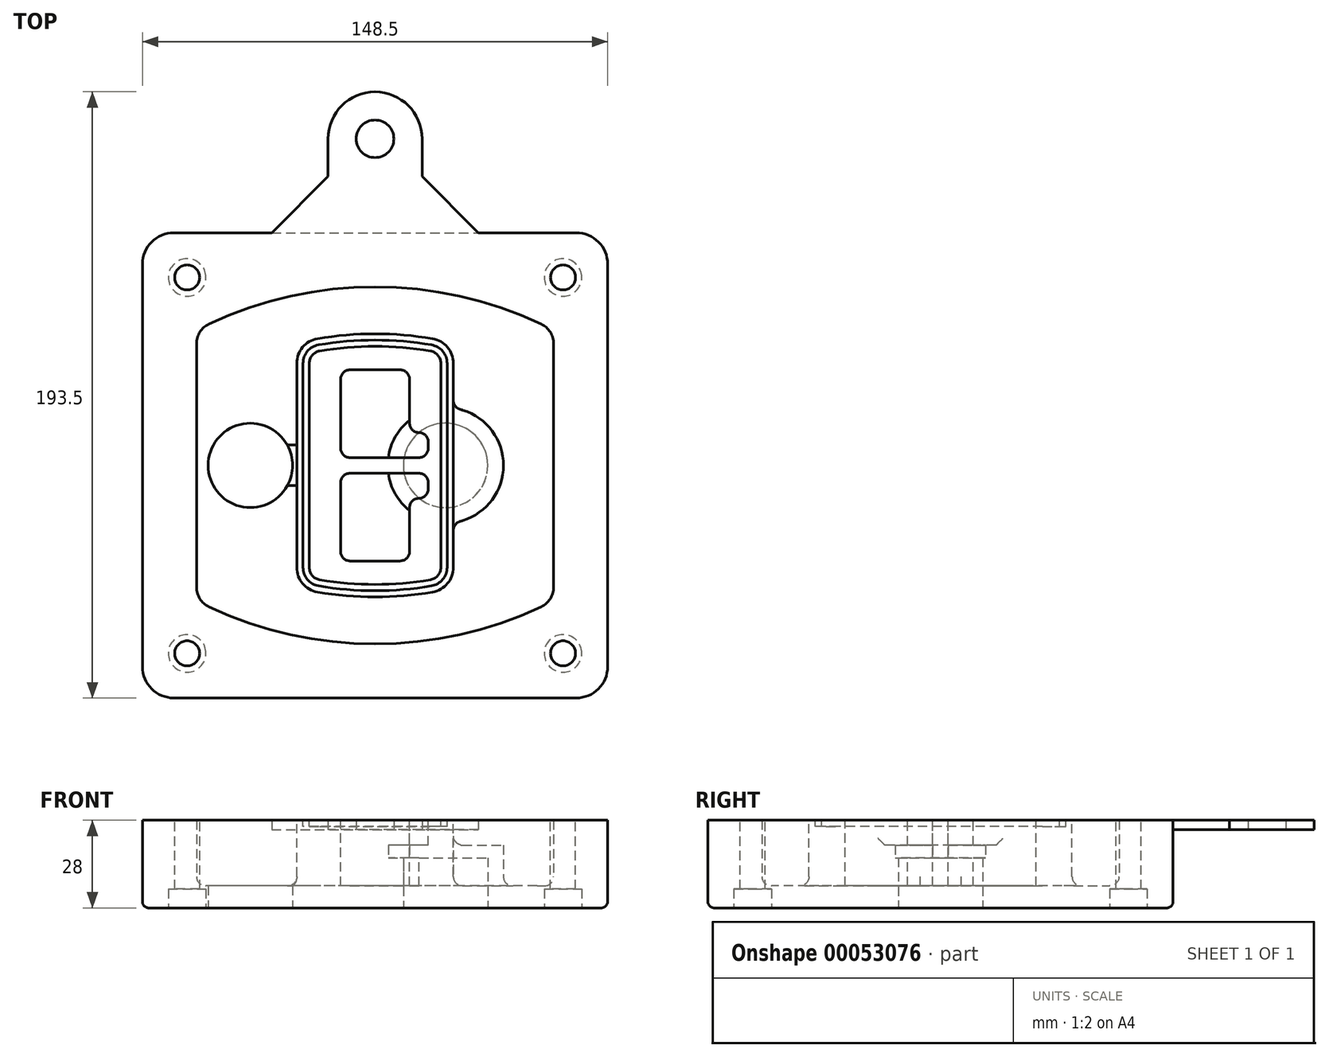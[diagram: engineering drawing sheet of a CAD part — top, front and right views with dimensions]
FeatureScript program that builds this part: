
annotation { "Feature Type Name" : "Feature", "Feature Type Description" : "" }
export const myFeature = defineFeature(function(context is Context, id is Id, definition is map)
    precondition{}
    {
        {
            var Q0;
            Q0=qCreatedBy(makeId("Top.planeOp"),FACE);
            var sketch = newSketch(context, id + "F0", { "sketchPlane" : qUnion([Q0])});
            skPoint(sketch, "E0.rect.middle", {"position": v(0, 0) * mm});
            skLineSegment(sketch, "E1.bottom", {"start": v(24.05, 28.38) * mm, "end": v(152.55, 28.38) * mm});
            skLineSegment(sketch, "E1.top", {"start": v(24.05, 176.88) * mm, "end": v(152.55, 176.88) * mm});
            skLineSegment(sketch, "E1.left", {"start": v(14.05, 38.38) * mm, "end": v(14.05, 166.88) * mm});
            skLineSegment(sketch, "E1.right", {"start": v(162.55, 38.38) * mm, "end": v(162.55, 166.88) * mm});
            skLineSegment(sketch, "E2", {"start": v(14.05, 176.88) * mm, "end": v(162.55, 28.38) * mm, "construction": true});
            skLineSegment(sketch, "E3", {"start": v(162.55, 176.88) * mm, "end": v(14.05, 28.38) * mm, "construction": true});
            skCircle(sketch, "E4", {"center": v(28.3, 162.63) * mm, "radius": 4 * mm});
            skCircle(sketch, "E5", {"center": v(148.3, 162.63) * mm, "radius": 4 * mm});
            skCircle(sketch, "E6", {"center": v(148.3, 42.63) * mm, "radius": 4 * mm});
            skCircle(sketch, "E7", {"center": v(28.3, 42.63) * mm, "radius": 4 * mm});
            skLineSegment(sketch, "E8", {"start": v(28.3, 162.63) * mm, "end": v(148.3, 162.63) * mm, "construction": true});
            skLineSegment(sketch, "E9", {"start": v(148.3, 162.63) * mm, "end": v(148.3, 42.63) * mm, "construction": true});
            skLineSegment(sketch, "E10", {"start": v(148.3, 42.63) * mm, "end": v(28.3, 42.63) * mm, "construction": true});
            skLineSegment(sketch, "E11", {"start": v(28.3, 42.63) * mm, "end": v(28.3, 162.63) * mm, "construction": true});
            skLineSegment(sketch, "E12", {"start": v(28.3, 141.46) * mm, "end": v(28.3, 63.8) * mm});
            skLineSegment(sketch, "E13", {"start": v(148.3, 141.46) * mm, "end": v(148.3, 63.8) * mm});
            skArc(sketch, "E14", {"start": v(142.56, 150.51) * mm, "mid": v(88.3, 162.63) * mm, "end": v(34.04, 150.51) * mm});
            skArc(sketch, "E15", {"start": v(34.04, 54.75) * mm, "mid": v(88.3, 42.63) * mm, "end": v(142.56, 54.75) * mm});
            skLineSegment(sketch, "E16", {"start": v(28.3, 102.63) * mm, "end": v(148.3, 102.63) * mm, "construction": true});
            skPoint(sketch, "E17.visualSharp", {"position": v(28.3, 57.63) * mm});
            skArc(sketch, "E17.filletArc", {"start": v(28.3, 63.8) * mm, "mid": v(29.86, 58.44) * mm, "end": v(34.04, 54.75) * mm});
            skPoint(sketch, "E18.visualSharp", {"position": v(28.3, 147.63) * mm});
            skArc(sketch, "E18.filletArc", {"start": v(34.04, 150.51) * mm, "mid": v(29.86, 146.82) * mm, "end": v(28.3, 141.46) * mm});
            skPoint(sketch, "E19.visualSharp", {"position": v(148.3, 147.63) * mm});
            skArc(sketch, "E19.filletArc", {"start": v(148.3, 141.46) * mm, "mid": v(146.74, 146.82) * mm, "end": v(142.56, 150.51) * mm});
            skPoint(sketch, "E20.visualSharp", {"position": v(148.3, 57.63) * mm});
            skArc(sketch, "E20.filletArc", {"start": v(142.56, 54.75) * mm, "mid": v(146.74, 58.44) * mm, "end": v(148.3, 63.8) * mm});
            skPoint(sketch, "E21.visualSharp", {"position": v(14.05, 176.88) * mm});
            skArc(sketch, "E21.filletArc", {"start": v(24.05, 176.88) * mm, "mid": v(16.98, 173.95) * mm, "end": v(14.05, 166.88) * mm});
            skPoint(sketch, "E22.visualSharp", {"position": v(162.55, 176.88) * mm});
            skArc(sketch, "E22.filletArc", {"start": v(162.55, 166.88) * mm, "mid": v(159.62, 173.95) * mm, "end": v(152.55, 176.88) * mm});
            skPoint(sketch, "E23.visualSharp", {"position": v(162.55, 28.38) * mm});
            skArc(sketch, "E23.filletArc", {"start": v(152.55, 28.38) * mm, "mid": v(159.62, 31.31) * mm, "end": v(162.55, 38.38) * mm});
            skPoint(sketch, "E24.visualSharp", {"position": v(14.05, 28.38) * mm});
            skArc(sketch, "E24.filletArc", {"start": v(14.05, 38.38) * mm, "mid": v(16.98, 31.31) * mm, "end": v(24.05, 28.38) * mm});
            skArc(sketch, "E25.0", {"start": v(145.3, 141.46) * mm, "mid": v(144.2, 145.22) * mm, "end": v(141.28, 147.8) * mm});
            skLineSegment(sketch, "E25.1", {"start": v(145.3, 141.46) * mm, "end": v(145.3, 63.8) * mm});
            skArc(sketch, "E25.2", {"start": v(141.28, 57.47) * mm, "mid": v(144.2, 60.05) * mm, "end": v(145.3, 63.8) * mm});
            skArc(sketch, "E25.3", {"start": v(35.32, 57.47) * mm, "mid": v(88.3, 45.63) * mm, "end": v(141.28, 57.47) * mm});
            skArc(sketch, "E25.4", {"start": v(31.3, 63.8) * mm, "mid": v(32.4, 60.05) * mm, "end": v(35.32, 57.47) * mm});
            skArc(sketch, "E25.5", {"start": v(141.28, 147.8) * mm, "mid": v(88.3, 159.63) * mm, "end": v(35.32, 147.8) * mm});
            skLineSegment(sketch, "E25.6", {"start": v(31.3, 141.46) * mm, "end": v(31.3, 63.8) * mm});
            skArc(sketch, "E25.7", {"start": v(35.32, 147.8) * mm, "mid": v(32.4, 145.22) * mm, "end": v(31.3, 141.46) * mm});
            skArc(sketch, "E26.0", {"start": v(32.34, 154.13) * mm, "mid": v(26.48, 148.97) * mm, "end": v(24.3, 141.46) * mm});
            skArc(sketch, "E26.1", {"start": v(144.26, 154.13) * mm, "mid": v(88.3, 166.63) * mm, "end": v(32.34, 154.13) * mm});
            skArc(sketch, "E26.2", {"start": v(152.3, 141.46) * mm, "mid": v(150.12, 148.97) * mm, "end": v(144.26, 154.13) * mm});
            skLineSegment(sketch, "E26.3", {"start": v(152.3, 141.46) * mm, "end": v(152.3, 63.8) * mm});
            skArc(sketch, "E26.4", {"start": v(144.26, 51.13) * mm, "mid": v(150.12, 56.3) * mm, "end": v(152.3, 63.8) * mm});
            skLineSegment(sketch, "E26.5", {"start": v(24.3, 141.46) * mm, "end": v(24.3, 63.8) * mm});
            skArc(sketch, "E26.6", {"start": v(32.34, 51.13) * mm, "mid": v(88.3, 38.63) * mm, "end": v(144.26, 51.13) * mm});
            skArc(sketch, "E26.7", {"start": v(24.3, 63.8) * mm, "mid": v(26.48, 56.3) * mm, "end": v(32.34, 51.13) * mm});
            skSolve(sketch);
        }
        {
            var Q0;
            Q0=makeQuery(id+"F0.imprint","IMPRINT",FACE,{"disambiguationData":[TD([[makeQuery(id+"F0.imprint","IMPRINT",EDGE,{"derivedFrom":sQuery(id+"F0.wireOp",EDGE,"E1.bottom")}),1.0]])]});
            var Q1;
            Q1=makeQuery(id+"F0.imprint","IMPRINT",FACE,{"disambiguationData":[TD([[makeQuery(id+"F0.imprint","IMPRINT",EDGE,{"derivedFrom":sQuery(id+"F0.wireOp",EDGE,"E12")}),1.0]])]});
            var Q2;
            Q2=makeQuery(id+"F0.imprint","IMPRINT",FACE,{"disambiguationData":[TD([[makeQuery(id+"F0.imprint","IMPRINT",EDGE,{"derivedFrom":sQuery(id+"F0.wireOp",EDGE,"E25.0")}),1.0]])]});
            var Q3;
            Q3=makeQuery(id+"F0.imprint","IMPRINT",FACE,{"disambiguationData":[TD([[makeQuery(id+"F0.imprint","IMPRINT",EDGE,{"derivedFrom":sQuery(id+"F0.wireOp",EDGE,"E12")}),-1.0]])]});
            extrude(context, id + "F1", {"entities" : qUnion([Q0, Q1, Q2, Q3]), "oppositeDirection" : true, "depth" : 25 * mm});
        }
        {
            var Q0;
            Q0=makeQuery(id+"F0.imprint","IMPRINT",FACE,{"disambiguationData":[TD([[makeQuery(id+"F0.imprint","IMPRINT",EDGE,{"derivedFrom":sQuery(id+"F0.wireOp",EDGE,"E12")}),1.0]])]});
            extrude(context, id + "F2", {"entities" : qUnion([Q0]), "operationType" : NewBodyOperationType.ADD, "depth" : 3 * mm});
        }
        {
            var Q0;
            Q0=makeQuery(id+"F0.imprint","IMPRINT",FACE,{"disambiguationData":[TD([[makeQuery(id+"F0.imprint","IMPRINT",EDGE,{"derivedFrom":sQuery(id+"F0.wireOp",EDGE,"E25.0")}),1.0]])]});
            extrude(context, id + "F3", {"entities" : qUnion([Q0]), "operationType" : NewBodyOperationType.REMOVE, "oppositeDirection" : true, "depth" : 18 * mm});
        }
        {
            var Q0;
            Q0=makeQuery(id+"F2.opExtrude","CAP_FACE",FACE,{"disambiguationData":[OSD([sQuery(id+"F0.wireOp",EDGE,"E12"),sQuery(id+"F0.wireOp",EDGE,"E13"),sQuery(id+"F0.wireOp",EDGE,"E14"),sQuery(id+"F0.wireOp",EDGE,"E15"),sQuery(id+"F0.wireOp",EDGE,"E17.filletArc"),sQuery(id+"F0.wireOp",EDGE,"E18.filletArc"),sQuery(id+"F0.wireOp",EDGE,"E19.filletArc"),sQuery(id+"F0.wireOp",EDGE,"E20.filletArc"),sQuery(id+"F0.wireOp",EDGE,"E25.0"),sQuery(id+"F0.wireOp",EDGE,"E25.1"),sQuery(id+"F0.wireOp",EDGE,"E25.2"),sQuery(id+"F0.wireOp",EDGE,"E25.3"),sQuery(id+"F0.wireOp",EDGE,"E25.4"),sQuery(id+"F0.wireOp",EDGE,"E25.5"),sQuery(id+"F0.wireOp",EDGE,"E25.6"),sQuery(id+"F0.wireOp",EDGE,"E25.7")])],"isStart":false});
            var sketch = newSketch(context, id + "F4", { "sketchPlane" : qUnion([Q0])});
            skArc(sketch, "E27.0", {"start": v(69.96, 62.18) * mm, "mid": v(88.3, 60.63) * mm, "end": v(106.64, 62.18) * mm});
            skArc(sketch, "E28.0", {"start": v(106.64, 143.09) * mm, "mid": v(88.3, 144.63) * mm, "end": v(69.96, 143.09) * mm});
            skLineSegment(sketch, "E29", {"start": v(63.3, 135.2) * mm, "end": v(63.3, 70.07) * mm});
            skLineSegment(sketch, "E30", {"start": v(113.3, 135.2) * mm, "end": v(113.3, 70.07) * mm});
            skLineSegment(sketch, "E31", {"start": v(63.3, 141.74) * mm, "end": v(113.3, 141.74) * mm, "construction": true});
            skLineSegment(sketch, "E32", {"start": v(63.3, 63.52) * mm, "end": v(113.3, 63.52) * mm, "construction": true});
            skPoint(sketch, "E33.visualSharp", {"position": v(63.3, 141.74) * mm});
            skArc(sketch, "E33.filletArc", {"start": v(69.96, 143.09) * mm, "mid": v(65.19, 140.36) * mm, "end": v(63.3, 135.2) * mm});
            skPoint(sketch, "E34.visualSharp", {"position": v(113.3, 141.74) * mm});
            skArc(sketch, "E34.filletArc", {"start": v(113.3, 135.2) * mm, "mid": v(111.41, 140.36) * mm, "end": v(106.64, 143.09) * mm});
            skPoint(sketch, "E35.visualSharp", {"position": v(113.3, 63.52) * mm});
            skArc(sketch, "E35.filletArc", {"start": v(106.64, 62.18) * mm, "mid": v(111.41, 64.9) * mm, "end": v(113.3, 70.07) * mm});
            skPoint(sketch, "E36.visualSharp", {"position": v(63.3, 63.52) * mm});
            skArc(sketch, "E36.filletArc", {"start": v(63.3, 70.07) * mm, "mid": v(65.19, 64.9) * mm, "end": v(69.96, 62.18) * mm});
            skArc(sketch, "E37.0", {"start": v(141.28, 147.8) * mm, "mid": v(88.3, 159.63) * mm, "end": v(35.32, 147.8) * mm});
            skArc(sketch, "E37.1", {"start": v(35.32, 147.8) * mm, "mid": v(32.4, 145.22) * mm, "end": v(31.3, 141.46) * mm});
            skLineSegment(sketch, "E37.2", {"start": v(31.3, 141.46) * mm, "end": v(31.3, 63.8) * mm});
            skArc(sketch, "E37.3", {"start": v(31.3, 63.8) * mm, "mid": v(32.4, 60.05) * mm, "end": v(35.32, 57.47) * mm});
            skArc(sketch, "E37.4", {"start": v(35.32, 57.47) * mm, "mid": v(88.3, 45.63) * mm, "end": v(141.28, 57.47) * mm});
            skArc(sketch, "E37.5", {"start": v(141.28, 57.47) * mm, "mid": v(144.2, 60.05) * mm, "end": v(145.3, 63.8) * mm});
            skLineSegment(sketch, "E37.6", {"start": v(145.3, 141.46) * mm, "end": v(145.3, 63.8) * mm});
            skArc(sketch, "E37.7", {"start": v(145.3, 141.46) * mm, "mid": v(144.2, 145.22) * mm, "end": v(141.28, 147.8) * mm});
            skLineSegment(sketch, "E38.0", {"start": v(111.3, 135.2) * mm, "end": v(111.3, 70.07) * mm});
            skArc(sketch, "E38.1", {"start": v(106.3, 64.15) * mm, "mid": v(109.88, 66.2) * mm, "end": v(111.3, 70.07) * mm});
            skArc(sketch, "E38.2", {"start": v(70.3, 64.15) * mm, "mid": v(88.3, 62.63) * mm, "end": v(106.3, 64.15) * mm});
            skArc(sketch, "E38.3", {"start": v(65.3, 70.07) * mm, "mid": v(66.72, 66.2) * mm, "end": v(70.3, 64.15) * mm});
            skLineSegment(sketch, "E38.4", {"start": v(65.3, 135.2) * mm, "end": v(65.3, 70.07) * mm});
            skArc(sketch, "E38.5", {"start": v(111.3, 135.2) * mm, "mid": v(109.88, 139.07) * mm, "end": v(106.3, 141.11) * mm});
            skArc(sketch, "E38.6", {"start": v(70.3, 141.11) * mm, "mid": v(66.72, 139.07) * mm, "end": v(65.3, 135.2) * mm});
            skArc(sketch, "E38.7", {"start": v(106.3, 141.11) * mm, "mid": v(88.3, 142.63) * mm, "end": v(70.3, 141.11) * mm});
            skArc(sketch, "E39.0", {"start": v(109.3, 135.2) * mm, "mid": v(108.36, 137.78) * mm, "end": v(105.97, 139.14) * mm});
            skLineSegment(sketch, "E39.1", {"start": v(109.3, 135.2) * mm, "end": v(109.3, 70.07) * mm});
            skArc(sketch, "E39.2", {"start": v(105.97, 66.12) * mm, "mid": v(108.36, 67.49) * mm, "end": v(109.3, 70.07) * mm});
            skArc(sketch, "E39.3", {"start": v(70.63, 66.12) * mm, "mid": v(88.3, 64.63) * mm, "end": v(105.97, 66.12) * mm});
            skArc(sketch, "E39.4", {"start": v(67.3, 70.07) * mm, "mid": v(68.24, 67.49) * mm, "end": v(70.63, 66.12) * mm});
            skArc(sketch, "E39.5", {"start": v(105.97, 139.14) * mm, "mid": v(88.3, 140.63) * mm, "end": v(70.63, 139.14) * mm});
            skLineSegment(sketch, "E39.6", {"start": v(67.3, 135.2) * mm, "end": v(67.3, 70.07) * mm});
            skArc(sketch, "E39.7", {"start": v(70.63, 139.14) * mm, "mid": v(68.24, 137.78) * mm, "end": v(67.3, 135.2) * mm});
            skLineSegment(sketch, "E40", {"start": v(63.3, 102.63) * mm, "end": v(113.3, 102.63) * mm, "construction": true});
            skLineSegment(sketch, "E41", {"start": v(77.3, 108.13) * mm, "end": v(77.3, 130.13) * mm});
            skLineSegment(sketch, "E42", {"start": v(80.3, 133.13) * mm, "end": v(96.3, 133.13) * mm});
            skLineSegment(sketch, "E43", {"start": v(99.3, 130.13) * mm, "end": v(99.3, 116.13) * mm});
            skLineSegment(sketch, "E44", {"start": v(102.3, 113.13) * mm, "end": v(102.3, 113.13) * mm});
            skLineSegment(sketch, "E45", {"start": v(105.3, 110.13) * mm, "end": v(105.3, 108.13) * mm});
            skLineSegment(sketch, "E46", {"start": v(102.3, 105.13) * mm, "end": v(80.3, 105.13) * mm});
            skPoint(sketch, "E47.visualSharp", {"position": v(77.3, 133.13) * mm});
            skArc(sketch, "E47.filletArc", {"start": v(80.3, 133.13) * mm, "mid": v(78.18, 132.25) * mm, "end": v(77.3, 130.13) * mm});
            skPoint(sketch, "E48.visualSharp", {"position": v(99.3, 133.13) * mm});
            skArc(sketch, "E48.filletArc", {"start": v(99.3, 130.13) * mm, "mid": v(98.42, 132.25) * mm, "end": v(96.3, 133.13) * mm});
            skPoint(sketch, "E49.visualSharp", {"position": v(99.3, 113.13) * mm});
            skArc(sketch, "E49.filletArc", {"start": v(99.3, 116.13) * mm, "mid": v(100.18, 114.01) * mm, "end": v(102.3, 113.13) * mm});
            skPoint(sketch, "E50.visualSharp", {"position": v(105.3, 113.13) * mm});
            skArc(sketch, "E50.filletArc", {"start": v(105.3, 110.13) * mm, "mid": v(104.42, 112.25) * mm, "end": v(102.3, 113.13) * mm});
            skPoint(sketch, "E51.visualSharp", {"position": v(105.3, 105.13) * mm});
            skArc(sketch, "E51.filletArc", {"start": v(102.3, 105.13) * mm, "mid": v(104.42, 106.01) * mm, "end": v(105.3, 108.13) * mm});
            skPoint(sketch, "E52.visualSharp", {"position": v(77.3, 105.13) * mm});
            skArc(sketch, "E52.filletArc", {"start": v(77.3, 108.13) * mm, "mid": v(78.18, 106.01) * mm, "end": v(80.3, 105.13) * mm});
            skLineSegment(sketch, "E53.0.MirrorCS", {"start": v(102.3, 100.13) * mm, "end": v(80.3, 100.13) * mm});
            skArc(sketch, "E54.0.MirrorCS", {"start": v(77.3, 97.13) * mm, "mid": v(78.18, 99.25) * mm, "end": v(80.3, 100.13) * mm});
            skLineSegment(sketch, "E55.0.MirrorCS", {"start": v(77.3, 97.13) * mm, "end": v(77.3, 75.13) * mm});
            skArc(sketch, "E56.0.MirrorCS", {"start": v(80.3, 72.13) * mm, "mid": v(78.18, 73.01) * mm, "end": v(77.3, 75.13) * mm});
            skLineSegment(sketch, "E57.0.MirrorCS", {"start": v(80.3, 72.13) * mm, "end": v(96.3, 72.13) * mm});
            skArc(sketch, "E58.0.MirrorCS", {"start": v(99.3, 75.13) * mm, "mid": v(98.42, 73.01) * mm, "end": v(96.3, 72.13) * mm});
            skLineSegment(sketch, "E59.0.MirrorCS", {"start": v(99.3, 75.13) * mm, "end": v(99.3, 89.13) * mm});
            skArc(sketch, "E60.0.MirrorCS", {"start": v(99.3, 89.13) * mm, "mid": v(100.18, 91.25) * mm, "end": v(102.3, 92.13) * mm});
            skArc(sketch, "E61.0.MirrorCS", {"start": v(105.3, 95.13) * mm, "mid": v(104.42, 93.01) * mm, "end": v(102.3, 92.13) * mm});
            skLineSegment(sketch, "E62.0.MirrorCS", {"start": v(105.3, 95.13) * mm, "end": v(105.3, 97.13) * mm});
            skArc(sketch, "E63.0.MirrorCS", {"start": v(102.3, 100.13) * mm, "mid": v(104.42, 99.25) * mm, "end": v(105.3, 97.13) * mm});
            skSolve(sketch);
        }
        {
            var Q0;
            Q0=makeQuery(id+"F4.imprint","IMPRINT",FACE,{"disambiguationData":[TD([[makeQuery(id+"F4.imprint","IMPRINT",EDGE,{"derivedFrom":sQuery(id+"F4.wireOp",EDGE,"E27.0")}),1.0]])]});
            var Q1;
            Q1=makeQuery(id+"F4.imprint","IMPRINT",FACE,{"disambiguationData":[TD([[makeQuery(id+"F4.imprint","IMPRINT",EDGE,{"derivedFrom":sQuery(id+"F4.wireOp",EDGE,"E38.0")}),-1.0]])]});
            var Q2;
            Q2=makeQuery(id+"F4.imprint","IMPRINT",FACE,{"disambiguationData":[TD([[makeQuery(id+"F4.imprint","IMPRINT",EDGE,{"derivedFrom":sQuery(id+"F4.wireOp",EDGE,"E39.0")}),1.0]])]});
            extrude(context, id + "F5", {"entities" : qUnion([Q0, Q1, Q2]), "operationType" : NewBodyOperationType.ADD, "endBound" : BoundingType.UP_TO_NEXT, "oppositeDirection" : true, "depth" : 25 * mm});
        }
        {
            var Q0;
            Q0=makeQuery(id+"F4.imprint","IMPRINT",FACE,{"disambiguationData":[TD([[makeQuery(id+"F4.imprint","IMPRINT",EDGE,{"derivedFrom":sQuery(id+"F4.wireOp",EDGE,"E38.0")}),-1.0]])]});
            extrude(context, id + "F6", {"entities" : qUnion([Q0]), "operationType" : NewBodyOperationType.REMOVE, "oppositeDirection" : true, "depth" : 2 * mm});
        }
        {
            var Q0;
            Q0=makeQuery(id+"F1.opExtrude","CAP_FACE",FACE,{"disambiguationData":[OSD([sQuery(id+"F0.wireOp",EDGE,"E1.bottom"),sQuery(id+"F0.wireOp",EDGE,"E1.top"),sQuery(id+"F0.wireOp",EDGE,"E1.left"),sQuery(id+"F0.wireOp",EDGE,"E1.right"),sQuery(id+"F0.wireOp",EDGE,"E4"),sQuery(id+"F0.wireOp",EDGE,"E5"),sQuery(id+"F0.wireOp",EDGE,"E6"),sQuery(id+"F0.wireOp",EDGE,"E7"),sQuery(id+"F0.wireOp",EDGE,"E21.filletArc"),sQuery(id+"F0.wireOp",EDGE,"E22.filletArc"),sQuery(id+"F0.wireOp",EDGE,"E23.filletArc"),sQuery(id+"F0.wireOp",EDGE,"E24.filletArc")])],"isStart":false});
            var sketch = newSketch(context, id + "F7", { "sketchPlane" : qUnion([Q0])});
            skCircle(sketch, "E64", {"center": v(110.8, -102.63) * mm, "radius": 13.47 * mm});
            skCircle(sketch, "E65", {"center": v(48.49, -102.63) * mm, "radius": 13.47 * mm});
            skLineSegment(sketch, "E66", {"start": v(162.55, -102.63) * mm, "end": v(14.05, -102.63) * mm});
            skCircle(sketch, "E67", {"center": v(110.8, -102.63) * mm, "radius": 18.47 * mm});
            skCircle(sketch, "E68", {"center": v(148.3, -162.63) * mm, "radius": 6 * mm});
            skCircle(sketch, "E69", {"center": v(28.3, -162.63) * mm, "radius": 6 * mm});
            skCircle(sketch, "E70", {"center": v(28.3, -42.63) * mm, "radius": 6 * mm});
            skCircle(sketch, "E71", {"center": v(148.3, -42.63) * mm, "radius": 6 * mm});
            skSolve(sketch);
        }
        {
            var Q0;
            {var subQ1=sQuery(id+"F7.wireOp",EDGE,"E66");var subQ4=sQuery(id+"F7.wireOp",EDGE,"E64");var subQ6=makeQuery(id+"F7.imprint","INTERSECT",VERTEX,{"disambiguationData":[OD(0.0)],"derivedFrom":[subQ4,subQ1]});Q0=makeQuery(id+"F7.imprint","IMPRINT",FACE,{"disambiguationData":[TD([[makeQuery(id+"F7.imprint","IMPRINT",EDGE,{"disambiguationData":[TD([[subQ6,-1.0]])],"derivedFrom":subQ4}),-1.0]])]});}
            var Q1;
            {var subQ0=sQuery(id+"F7.wireOp",EDGE,"E66");var subQ1=sQuery(id+"F7.wireOp",EDGE,"E64");var subQ3=makeQuery(id+"F7.imprint","INTERSECT",VERTEX,{"disambiguationData":[OD(0.0)],"derivedFrom":[subQ1,subQ0]});Q1=makeQuery(id+"F7.imprint","IMPRINT",FACE,{"disambiguationData":[TD([[makeQuery(id+"F7.imprint","IMPRINT",EDGE,{"disambiguationData":[TD([[subQ3,-1.0]])],"derivedFrom":subQ1}),1.0]])]});}
            var Q2;
            {var subQ0=sQuery(id+"F7.wireOp",EDGE,"E66");var subQ1=sQuery(id+"F7.wireOp",EDGE,"E64");var subQ3=makeQuery(id+"F7.imprint","INTERSECT",VERTEX,{"disambiguationData":[OD(0.0)],"derivedFrom":[subQ1,subQ0]});Q2=makeQuery(id+"F7.imprint","IMPRINT",FACE,{"disambiguationData":[TD([[makeQuery(id+"F7.imprint","IMPRINT",EDGE,{"disambiguationData":[TD([[subQ3,1.0]])],"derivedFrom":subQ1}),1.0]])]});}
            var Q3;
            {var subQ1=sQuery(id+"F7.wireOp",EDGE,"E66");var subQ4=sQuery(id+"F7.wireOp",EDGE,"E64");var subQ6=makeQuery(id+"F7.imprint","INTERSECT",VERTEX,{"disambiguationData":[OD(0.0)],"derivedFrom":[subQ4,subQ1]});Q3=makeQuery(id+"F7.imprint","IMPRINT",FACE,{"disambiguationData":[TD([[makeQuery(id+"F7.imprint","IMPRINT",EDGE,{"disambiguationData":[TD([[subQ6,1.0]])],"derivedFrom":subQ4}),-1.0]])]});}
            extrude(context, id + "F8", {"entities" : qUnion([Q0, Q1, Q2, Q3]), "operationType" : NewBodyOperationType.ADD, "oppositeDirection" : true, "depth" : 20 * mm});
        }
        {
            var Q0;
            {var subQ0=sQuery(id+"F7.wireOp",EDGE,"E66");var subQ1=sQuery(id+"F7.wireOp",EDGE,"E64");var subQ3=makeQuery(id+"F7.imprint","INTERSECT",VERTEX,{"disambiguationData":[OD(0.0)],"derivedFrom":[subQ1,subQ0]});Q0=makeQuery(id+"F7.imprint","IMPRINT",FACE,{"disambiguationData":[TD([[makeQuery(id+"F7.imprint","IMPRINT",EDGE,{"disambiguationData":[TD([[subQ3,-1.0]])],"derivedFrom":subQ1}),1.0]])]});}
            var Q1;
            {var subQ0=sQuery(id+"F7.wireOp",EDGE,"E66");var subQ1=sQuery(id+"F7.wireOp",EDGE,"E64");var subQ3=makeQuery(id+"F7.imprint","INTERSECT",VERTEX,{"disambiguationData":[OD(0.0)],"derivedFrom":[subQ1,subQ0]});Q1=makeQuery(id+"F7.imprint","IMPRINT",FACE,{"disambiguationData":[TD([[makeQuery(id+"F7.imprint","IMPRINT",EDGE,{"disambiguationData":[TD([[subQ3,1.0]])],"derivedFrom":subQ1}),1.0]])]});}
            extrude(context, id + "F9", {"entities" : qUnion([Q0, Q1]), "operationType" : NewBodyOperationType.REMOVE, "oppositeDirection" : true, "depth" : 16 * mm});
        }
        {
            var Q0;
            {var subQ0=sQuery(id+"F7.wireOp",EDGE,"E66");var subQ1=sQuery(id+"F7.wireOp",EDGE,"E65");var subQ3=makeQuery(id+"F7.imprint","INTERSECT",VERTEX,{"disambiguationData":[OD(0.0)],"derivedFrom":[subQ1,subQ0]});Q0=makeQuery(id+"F7.imprint","IMPRINT",FACE,{"disambiguationData":[TD([[makeQuery(id+"F7.imprint","IMPRINT",EDGE,{"disambiguationData":[TD([[subQ3,-1.0]])],"derivedFrom":subQ1}),1.0]])]});}
            var Q1;
            {var subQ0=sQuery(id+"F7.wireOp",EDGE,"E66");var subQ1=sQuery(id+"F7.wireOp",EDGE,"E65");var subQ3=makeQuery(id+"F7.imprint","INTERSECT",VERTEX,{"disambiguationData":[OD(0.0)],"derivedFrom":[subQ1,subQ0]});Q1=makeQuery(id+"F7.imprint","IMPRINT",FACE,{"disambiguationData":[TD([[makeQuery(id+"F7.imprint","IMPRINT",EDGE,{"disambiguationData":[TD([[subQ3,1.0]])],"derivedFrom":subQ1}),1.0]])]});}
            extrude(context, id + "F10", {"entities" : qUnion([Q0, Q1]), "operationType" : NewBodyOperationType.REMOVE, "oppositeDirection" : true, "depth" : 25 * mm});
        }
        {
            var Q0;
            Q0=makeQuery(id+"F7.imprint","IMPRINT",FACE,{"disambiguationData":[TD([[makeQuery(id+"F7.imprint","IMPRINT",EDGE,{"derivedFrom":sQuery(id+"F7.wireOp",EDGE,"E68")}),1.0]])]});
            var Q1;
            Q1=makeQuery(id+"F7.imprint","IMPRINT",FACE,{"disambiguationData":[TD([[makeQuery(id+"F7.imprint","IMPRINT",EDGE,{"derivedFrom":makeQuery(id+"F1.opExtrude","CAP_EDGE",EDGE,{"disambiguationData":[OSD([sQuery(id+"F0.wireOp",EDGE,"E5")])],"isStart":false})}),-1.0]])]});
            var Q2;
            Q2=makeQuery(id+"F7.imprint","IMPRINT",FACE,{"disambiguationData":[TD([[makeQuery(id+"F7.imprint","IMPRINT",EDGE,{"derivedFrom":sQuery(id+"F7.wireOp",EDGE,"E69")}),1.0]])]});
            var Q3;
            Q3=makeQuery(id+"F7.imprint","IMPRINT",FACE,{"disambiguationData":[TD([[makeQuery(id+"F7.imprint","IMPRINT",EDGE,{"derivedFrom":makeQuery(id+"F1.opExtrude","CAP_EDGE",EDGE,{"disambiguationData":[OSD([sQuery(id+"F0.wireOp",EDGE,"E4")])],"isStart":false})}),-1.0]])]});
            var Q4;
            Q4=makeQuery(id+"F7.imprint","IMPRINT",FACE,{"disambiguationData":[TD([[makeQuery(id+"F7.imprint","IMPRINT",EDGE,{"derivedFrom":sQuery(id+"F7.wireOp",EDGE,"E70")}),1.0]])]});
            var Q5;
            Q5=makeQuery(id+"F7.imprint","IMPRINT",FACE,{"disambiguationData":[TD([[makeQuery(id+"F7.imprint","IMPRINT",EDGE,{"derivedFrom":makeQuery(id+"F1.opExtrude","CAP_EDGE",EDGE,{"disambiguationData":[OSD([sQuery(id+"F0.wireOp",EDGE,"E7")])],"isStart":false})}),-1.0]])]});
            var Q6;
            Q6=makeQuery(id+"F7.imprint","IMPRINT",FACE,{"disambiguationData":[TD([[makeQuery(id+"F7.imprint","IMPRINT",EDGE,{"derivedFrom":sQuery(id+"F7.wireOp",EDGE,"E71")}),1.0]])]});
            var Q7;
            Q7=makeQuery(id+"F7.imprint","IMPRINT",FACE,{"disambiguationData":[TD([[makeQuery(id+"F7.imprint","IMPRINT",EDGE,{"derivedFrom":makeQuery(id+"F1.opExtrude","CAP_EDGE",EDGE,{"disambiguationData":[OSD([sQuery(id+"F0.wireOp",EDGE,"E6")])],"isStart":false})}),-1.0]])]});
            extrude(context, id + "F11", {"entities" : qUnion([Q0, Q1, Q2, Q3, Q4, Q5, Q6, Q7]), "operationType" : NewBodyOperationType.REMOVE, "oppositeDirection" : true, "depth" : 6 * mm});
        }
        {
            var Q0;
            Q0=makeQuery(id+"F9.boolean.opBoolean","COPY",FACE,{"derivedFrom":makeQuery(id+"F9.opExtrude","CAP_FACE",FACE,{"disambiguationData":[OSD([sQuery(id+"F7.wireOp",EDGE,"E64")])],"isStart":false})});
            var sketch = newSketch(context, id + "F12", { "sketchPlane" : qUnion([Q0])});
            skArc(sketch, "E72.0", {"start": v(99.3, -88.19) * mm, "mid": v(94.75, -93.5) * mm, "end": v(92.5, -100.13) * mm});
            skArc(sketch, "E72.1", {"start": v(92.5, -105.13) * mm, "mid": v(94.75, -111.76) * mm, "end": v(99.3, -117.08) * mm});
            skLineSegment(sketch, "E73", {"start": v(92.5, -105.13) * mm, "end": v(102.3, -105.13) * mm});
            skLineSegment(sketch, "E74.0", {"start": v(102.3, -100.13) * mm, "end": v(92.5, -100.13) * mm});
            skArc(sketch, "E74.1", {"start": v(102.3, -100.13) * mm, "mid": v(104.42, -99.25) * mm, "end": v(105.3, -97.13) * mm});
            skLineSegment(sketch, "E74.2", {"start": v(105.3, -95.13) * mm, "end": v(105.3, -97.13) * mm});
            skArc(sketch, "E74.3", {"start": v(105.3, -95.13) * mm, "mid": v(104.42, -93.01) * mm, "end": v(102.3, -92.13) * mm});
            skArc(sketch, "E74.4", {"start": v(99.3, -89.13) * mm, "mid": v(100.18, -91.25) * mm, "end": v(102.3, -92.13) * mm});
            skLineSegment(sketch, "E74.5", {"start": v(99.3, -88.19) * mm, "end": v(99.3, -89.13) * mm});
            skLineSegment(sketch, "E74.7", {"start": v(102.3, -105.13) * mm, "end": v(92.5, -105.13) * mm});
            skArc(sketch, "E74.8", {"start": v(102.3, -105.13) * mm, "mid": v(104.42, -106.01) * mm, "end": v(105.3, -108.13) * mm});
            skLineSegment(sketch, "E74.9", {"start": v(105.3, -110.13) * mm, "end": v(105.3, -108.13) * mm});
            skArc(sketch, "E74.10", {"start": v(105.3, -110.13) * mm, "mid": v(104.42, -112.25) * mm, "end": v(102.3, -113.13) * mm});
            skArc(sketch, "E74.11", {"start": v(99.3, -116.13) * mm, "mid": v(100.18, -114.01) * mm, "end": v(102.3, -113.13) * mm});
            skLineSegment(sketch, "E74.12", {"start": v(99.3, -117.08) * mm, "end": v(99.3, -116.13) * mm});
            skPoint(sketch, "E75.orphan", {"position": v(99.3, -130.13) * mm});
            skPoint(sketch, "E76.orphan", {"position": v(80.3, -105.13) * mm});
            skPoint(sketch, "E77.orphan", {"position": v(80.3, -100.13) * mm});
            skPoint(sketch, "E78.orphan", {"position": v(99.3, -75.13) * mm});
            skSolve(sketch);
        }
        {
            var Q0;
            {var subQ7=sQuery(id+"F12.wireOp",EDGE,"E72.0");var subQ14=sQuery(id+"F12.wireOp",EDGE,"E72.1");var subQ16=sQuery(id+"F12.wireOp",EDGE,"E74.1");var subQ18=sQuery(id+"F12.wireOp",EDGE,"E74.8");Q0=qUnion([makeQuery(id+"F12.imprint","IMPRINT",FACE,{"disambiguationData":[TD([[makeQuery(id+"F12.imprint","IMPRINT",EDGE,{"derivedFrom":subQ7}),1.0]])]}),makeQuery(id+"F12.imprint","IMPRINT",FACE,{"disambiguationData":[TD([[makeQuery(id+"F12.imprint","IMPRINT",EDGE,{"derivedFrom":subQ14}),1.0]])]}),makeQuery(id+"F12.imprint","IMPRINT",FACE,{"disambiguationData":[TD([[makeQuery(id+"F12.imprint","IMPRINT",EDGE,{"derivedFrom":subQ16}),1.0]])]}),makeQuery(id+"F12.imprint","IMPRINT",FACE,{"disambiguationData":[TD([[makeQuery(id+"F12.imprint","IMPRINT",EDGE,{"derivedFrom":subQ18}),-1.0]])]})]);}
            var Q1;
            Q1=makeQuery(id+"F5.boolean.opBoolean","SPLIT",FACE,{"disambiguationData":[TD([makeQuery(id+"F5.opExtrude","SWEPT_FACE",FACE,{"disambiguationData":[OSD([sQuery(id+"F4.wireOp",EDGE,"E41")])]})])],"derivedFrom":makeQuery(id+"F3.boolean.opBoolean","COPY",FACE,{"derivedFrom":makeQuery(id+"F3.opExtrude","CAP_FACE",FACE,{"disambiguationData":[OSD([sQuery(id+"F0.wireOp",EDGE,"E25.0"),sQuery(id+"F0.wireOp",EDGE,"E25.1"),sQuery(id+"F0.wireOp",EDGE,"E25.2"),sQuery(id+"F0.wireOp",EDGE,"E25.3"),sQuery(id+"F0.wireOp",EDGE,"E25.4"),sQuery(id+"F0.wireOp",EDGE,"E25.5"),sQuery(id+"F0.wireOp",EDGE,"E25.6"),sQuery(id+"F0.wireOp",EDGE,"E25.7")])],"isStart":false})})});
            extrude(context, id + "F13", {"entities" : qUnion([Q0]), "operationType" : NewBodyOperationType.REMOVE, "endBound" : BoundingType.UP_TO_SURFACE, "endBoundEntityFace" : qUnion([Q1]), "depth" : 25 * mm});
        }
        {
            var Q0;
            Q0=makeQuery(id+"F3.boolean.opBoolean","COPY",EDGE,{"derivedFrom":makeQuery(id+"F3.opExtrude","CAP_EDGE",EDGE,{"disambiguationData":[OSD([sQuery(id+"F0.wireOp",EDGE,"E25.6")])],"isStart":false})});
            var Q1;
            Q1=makeQuery(id+"F8.boolean.opBoolean","INTERSECT",EDGE,{"derivedFrom":[makeQuery(id+"F5.opExtrude","SWEPT_FACE",FACE,{"disambiguationData":[OSD([sQuery(id+"F4.wireOp",EDGE,"E30")])]}),makeQuery(id+"F8.opExtrude","CAP_FACE",FACE,{"disambiguationData":[OSD([sQuery(id+"F7.wireOp",EDGE,"E67")])],"isStart":false})]});
            var Q2;
            Q2=makeQuery(id+"F8.boolean.opBoolean","INTERSECT",EDGE,{"disambiguationData":[OD(1.0)],"derivedFrom":[makeQuery(id+"F5.opExtrude","SWEPT_FACE",FACE,{"disambiguationData":[OSD([sQuery(id+"F4.wireOp",EDGE,"E30")])]}),makeQuery(id+"F8.opExtrude","SWEPT_FACE",FACE,{"disambiguationData":[OSD([sQuery(id+"F7.wireOp",EDGE,"E67")])]})]});
            var Q3;
            {var subQ0=sQuery(id+"F4.wireOp",EDGE,"E30");Q3=makeQuery(id+"F8.boolean.opBoolean","SPLIT",EDGE,{"disambiguationData":[TD([makeQuery(id+"F5.opExtrude","SWEPT_FACE",FACE,{"disambiguationData":[OSD([sQuery(id+"F4.wireOp",EDGE,"E35.filletArc")])]})])],"derivedFrom":makeQuery(id+"F5.opExtrude","CAP_EDGE",EDGE,{"disambiguationData":[OSD([subQ0])],"isStart":false})});}
            var Q4;
            {var subQ0=sQuery(id+"F0.wireOp",EDGE,"E25.7");var subQ1=sQuery(id+"F0.wireOp",EDGE,"E25.1");var subQ2=sQuery(id+"F0.wireOp",EDGE,"E25.6");var subQ3=sQuery(id+"F0.wireOp",EDGE,"E25.5");var subQ4=sQuery(id+"F0.wireOp",EDGE,"E25.4");var subQ5=sQuery(id+"F0.wireOp",EDGE,"E25.0");var subQ6=sQuery(id+"F0.wireOp",EDGE,"E25.2");var subQ7=sQuery(id+"F0.wireOp",EDGE,"E25.3");Q4=makeQuery(id+"F8.boolean.opBoolean","INTERSECT",EDGE,{"derivedFrom":[makeQuery(id+"F5.boolean.opBoolean","SPLIT",FACE,{"disambiguationData":[TD([makeQuery(id+"F2.opExtrude","SWEPT_FACE",FACE,{"disambiguationData":[OSD([subQ5])]})])],"derivedFrom":makeQuery(id+"F3.boolean.opBoolean","COPY",FACE,{"derivedFrom":makeQuery(id+"F3.opExtrude","CAP_FACE",FACE,{"disambiguationData":[OSD([subQ5,subQ1,subQ6,subQ7,subQ4,subQ3,subQ2,subQ0])],"isStart":false})})}),makeQuery(id+"F8.opExtrude","SWEPT_FACE",FACE,{"disambiguationData":[OSD([sQuery(id+"F7.wireOp",EDGE,"E67")])]})]});}
            var Q5;
            Q5=makeQuery(id+"F8.boolean.opBoolean","INTERSECT",EDGE,{"disambiguationData":[OD(0.0)],"derivedFrom":[makeQuery(id+"F5.opExtrude","SWEPT_FACE",FACE,{"disambiguationData":[OSD([sQuery(id+"F4.wireOp",EDGE,"E30")])]}),makeQuery(id+"F8.opExtrude","SWEPT_FACE",FACE,{"disambiguationData":[OSD([sQuery(id+"F7.wireOp",EDGE,"E67")])]})]});
            fillet(context, id + "F14", {"entities" : qUnion([Q0, Q1, Q2, Q3, Q4, Q5]), "radius" : 3 * mm, "tangentPropagation" : true, "allowEdgeOverflow" : false});
        }
        {
            var Q0;
            Q0=makeQuery(id+"F1.opExtrude","CAP_EDGE",EDGE,{"disambiguationData":[OSD([sQuery(id+"F0.wireOp",EDGE,"E1.bottom")])],"isStart":false});
            fillet(context, id + "F15", {"entities" : qUnion([Q0]), "radius" : 2 * mm, "tangentPropagation" : true, "allowEdgeOverflow" : false});
        }
        {
            var Q0;
            {var subQ0=sQuery(id+"F0.wireOp",EDGE,"E1.bottom");var subQ1=sQuery(id+"F0.wireOp",EDGE,"E1.top");var subQ2=sQuery(id+"F0.wireOp",EDGE,"E1.left");var subQ3=sQuery(id+"F0.wireOp",EDGE,"E1.right");var subQ4=sQuery(id+"F0.wireOp",EDGE,"E4");var subQ5=sQuery(id+"F0.wireOp",EDGE,"E5");var subQ6=sQuery(id+"F0.wireOp",EDGE,"E6");var subQ7=sQuery(id+"F0.wireOp",EDGE,"E7");var subQ8=sQuery(id+"F0.wireOp",EDGE,"E21.filletArc");var subQ9=sQuery(id+"F0.wireOp",EDGE,"E22.filletArc");var subQ10=sQuery(id+"F0.wireOp",EDGE,"E23.filletArc");var subQ11=sQuery(id+"F0.wireOp",EDGE,"E24.filletArc");Q0=makeQuery(id+"F2.boolean.opBoolean","SPLIT",FACE,{"disambiguationData":[TD([makeQuery(id+"F1.opExtrude","SWEPT_FACE",FACE,{"disambiguationData":[OSD([subQ0])]})])],"derivedFrom":makeQuery(id+"F1.opExtrude","CAP_FACE",FACE,{"disambiguationData":[OSD([subQ0,subQ1,subQ2,subQ3,subQ4,subQ5,subQ6,subQ7,subQ8,subQ9,subQ10,subQ11])],"isStart":true})});}
            var sketch = newSketch(context, id + "F16", { "sketchPlane" : qUnion([Q0])});
            skLineSegment(sketch, "E79", {"start": v(55.3, 176.88) * mm, "end": v(73.3, 194.88) * mm});
            skLineSegment(sketch, "E80", {"start": v(121.3, 176.88) * mm, "end": v(103.3, 194.88) * mm});
            skLineSegment(sketch, "E81", {"start": v(73.3, 194.88) * mm, "end": v(73.3, 206.88) * mm});
            skLineSegment(sketch, "E82", {"start": v(103.3, 194.88) * mm, "end": v(103.3, 206.88) * mm});
            skArc(sketch, "E83", {"start": v(103.3, 206.88) * mm, "mid": v(88.3, 221.88) * mm, "end": v(73.3, 206.88) * mm});
            skCircle(sketch, "E84", {"center": v(88.3, 206.88) * mm, "radius": 6 * mm});
            skLineSegment(sketch, "E85", {"start": v(88.3, 206.88) * mm, "end": v(88.3, 176.88) * mm, "construction": true});
            skLineSegment(sketch, "E86", {"start": v(14.05, 102.63) * mm, "end": v(162.55, 102.63) * mm, "construction": true});
            skArc(sketch, "E87.MirrorCS", {"start": v(103.3, -1.62) * mm, "mid": v(88.3, -16.62) * mm, "end": v(73.3, -1.62) * mm});
            skLineSegment(sketch, "E88.MirrorCS", {"start": v(103.3, 10.38) * mm, "end": v(103.3, -1.62) * mm});
            skCircle(sketch, "E89.MirrorC", {"center": v(88.3, -1.62) * mm, "radius": 6 * mm});
            skLineSegment(sketch, "E90.MirrorCS", {"start": v(73.3, 10.38) * mm, "end": v(73.3, -1.62) * mm});
            skLineSegment(sketch, "E91.MirrorCS", {"start": v(121.3, 28.38) * mm, "end": v(103.3, 10.38) * mm});
            skLineSegment(sketch, "E92.MirrorCS", {"start": v(88.3, -1.62) * mm, "end": v(88.3, 28.38) * mm, "construction": true});
            skLineSegment(sketch, "E93.MirrorCS", {"start": v(55.3, 28.38) * mm, "end": v(73.3, 10.38) * mm});
            skSolve(sketch);
        }
        {
            var Q0;
            {var subQ0=sQuery(id+"F16.wireOp",EDGE,"E79");Q0=makeQuery(id+"F16.imprint","IMPRINT",FACE,{"disambiguationData":[TD([[makeQuery(id+"F16.imprint","IMPRINT",EDGE,{"derivedFrom":subQ0}),-1.0]])]});}
            var Q1;
            Q1=makeQuery(id+"F16.imprint","IMPRINT",FACE,{"disambiguationData":[TD([[makeQuery(id+"F16.imprint","IMPRINT",EDGE,{"derivedFrom":makeQuery(id+"F1.opExtrude","CAP_EDGE",EDGE,{"disambiguationData":[OSD([sQuery(id+"F0.wireOp",EDGE,"E1.left")])],"isStart":true})}),-1.0]])]});
            var Q2;
            Q2=makeQuery(id+"F16.imprint","IMPRINT",FACE,{"disambiguationData":[TD([[makeQuery(id+"F16.imprint","IMPRINT",EDGE,{"derivedFrom":sQuery(id+"F16.wireOp",EDGE,"E87.MirrorCS")}),-1.0]])]});
            var Q3;
            Q3=makeQuery(id+"F2.opExtrude","CAP_FACE",FACE,{"disambiguationData":[OSD([sQuery(id+"F0.wireOp",EDGE,"E12"),sQuery(id+"F0.wireOp",EDGE,"E13"),sQuery(id+"F0.wireOp",EDGE,"E14"),sQuery(id+"F0.wireOp",EDGE,"E15"),sQuery(id+"F0.wireOp",EDGE,"E17.filletArc"),sQuery(id+"F0.wireOp",EDGE,"E18.filletArc"),sQuery(id+"F0.wireOp",EDGE,"E19.filletArc"),sQuery(id+"F0.wireOp",EDGE,"E20.filletArc"),sQuery(id+"F0.wireOp",EDGE,"E25.0"),sQuery(id+"F0.wireOp",EDGE,"E25.1"),sQuery(id+"F0.wireOp",EDGE,"E25.2"),sQuery(id+"F0.wireOp",EDGE,"E25.3"),sQuery(id+"F0.wireOp",EDGE,"E25.4"),sQuery(id+"F0.wireOp",EDGE,"E25.5"),sQuery(id+"F0.wireOp",EDGE,"E25.6"),sQuery(id+"F0.wireOp",EDGE,"E25.7")])],"isStart":false});
            extrude(context, id + "F17", {"entities" : qUnion([Q0, Q1, Q2]), "operationType" : NewBodyOperationType.ADD, "endBound" : BoundingType.UP_TO_SURFACE, "endBoundEntityFace" : qUnion([Q3]), "depth" : 25 * mm});
        }
    });
